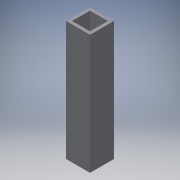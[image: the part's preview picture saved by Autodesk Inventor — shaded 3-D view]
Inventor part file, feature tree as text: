
AUTODESK INVENTOR PART (.ipt)
format: ipt  version: 2016 (Build 200138000, 138)  size: 122,880 bytes
history: native  units: in
note: dims shown in document units (in); Inventor stores cm internally (conversion verified against a paired STEP export)
features: extrude x2, sketch x2
ambient origin geometry x8: Origin, YZ Plane, XZ Plane, XY Plane, X Axis, Y Axis, Z Axis, Center Point
bodies: Solid1 (feature_tree)
feature tree (4):
  extrude  "Extrusion1"  Depth=1.0in
  extrude  "Extrusion2"  Depth=8.0in TaperAngle=0.0deg
  sketch  "Sketch1"  dims[d0=1.0in d1=1.0in]
  sketch  "Sketch2"  dims[d2=0.125in d3=8.0in d4=0.0in d5=0.2031in d6=0.2031in d7=1.875in d8=0.5in d9=0.5in d10=0.5in d11=1.0in d12=0.0in d13=0.75in d14=0.9375in d15=0.5in d16=0.2656in d17=0.5in d18=0.5in]
